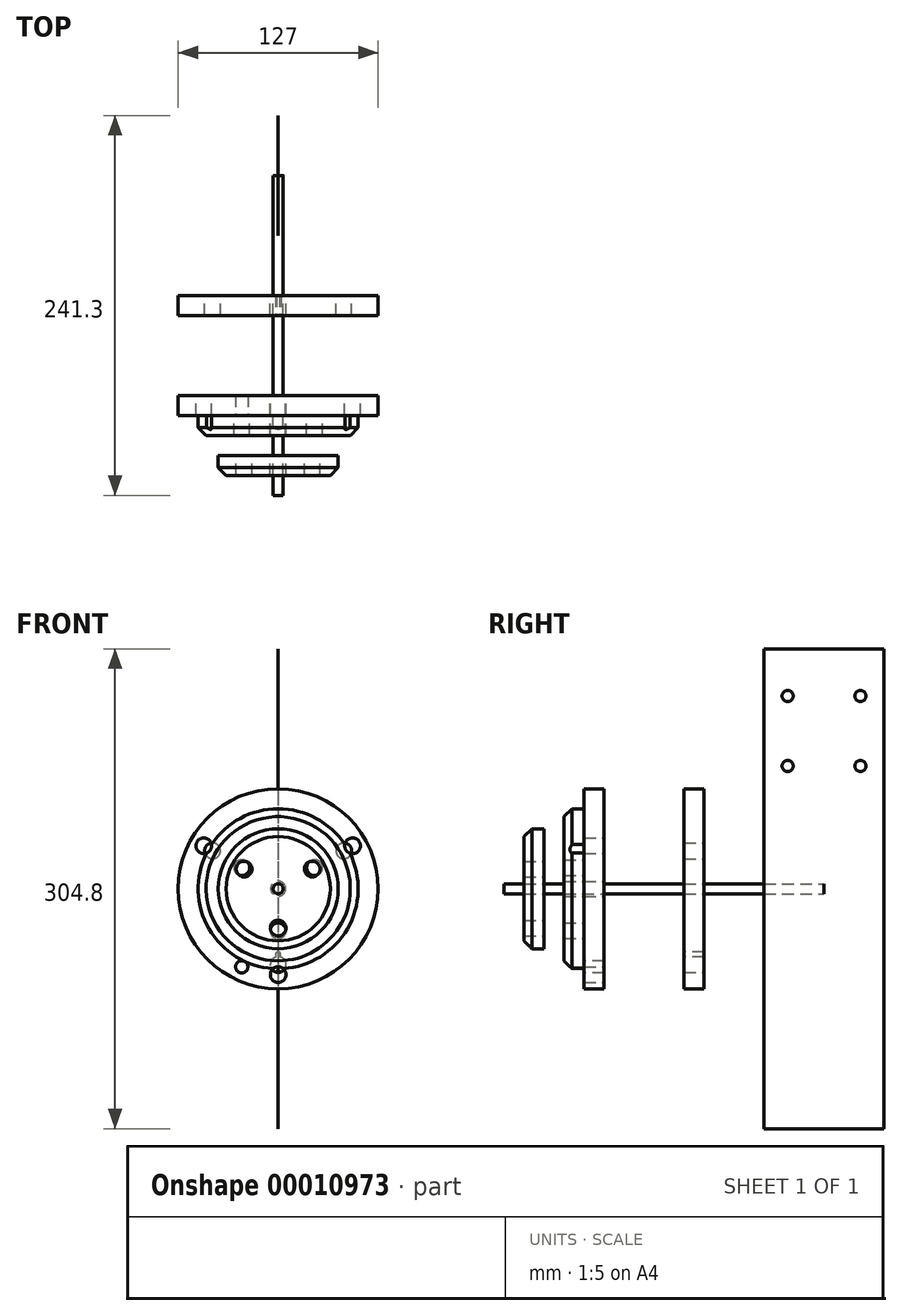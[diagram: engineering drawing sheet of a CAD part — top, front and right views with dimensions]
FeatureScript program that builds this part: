
annotation { "Feature Type Name" : "Feature", "Feature Type Description" : "" }
export const myFeature = defineFeature(function(context is Context, id is Id, definition is map)
    precondition{}
    {
        {
            var Q0;
            Q0=qCreatedBy(makeId("Right.planeOp"),FACE);
            var sketch = newSketch(context, id + "F0", { "sketchPlane" : qUnion([Q0])});
            skLineSegment(sketch, "E0.rect.bottom", {"start": v(-38.1, 152.4) * mm, "end": v(38.1, 152.4) * mm});
            skLineSegment(sketch, "E0.rect.top", {"start": v(-38.1, -152.4) * mm, "end": v(38.1, -152.4) * mm});
            skLineSegment(sketch, "E0.rect.left", {"start": v(-38.1, 152.4) * mm, "end": v(-38.1, -152.4) * mm});
            skLineSegment(sketch, "E0.rect.right", {"start": v(38.1, 152.4) * mm, "end": v(38.1, -152.4) * mm});
            skPoint(sketch, "E0.rect.middle", {"position": v(0, 0) * mm});
            skLineSegment(sketch, "E1", {"start": v(-38.1, 122.4) * mm, "end": v(38.1, 122.4) * mm, "construction": true});
            skCircle(sketch, "E2", {"center": v(-23.1, 122.4) * mm, "radius": 3.56 * mm});
            skCircle(sketch, "E3", {"center": v(23.1, 122.4) * mm, "radius": 3.56 * mm});
            skCircle(sketch, "E4.0.1.0", {"center": v(-23.1, 77.95) * mm, "radius": 3.56 * mm});
            skCircle(sketch, "E4.0.1.1", {"center": v(23.1, 77.95) * mm, "radius": 3.56 * mm});
            skLineSegment(sketch, "E4.direction1", {"start": v(-23.1, 122.4) * mm, "end": v(1.9, 122.4) * mm, "construction": true});
            skLineSegment(sketch, "E4.direction2", {"start": v(-23.1, 122.4) * mm, "end": v(-23.1, 77.95) * mm, "construction": true});
            skSolve(sketch);
        }
        {
            var Q0;
            Q0=makeQuery(id+"F0.imprint","IMPRINT",FACE,{"disambiguationData":[TD([[makeQuery(id+"F0.imprint","IMPRINT",EDGE,{"derivedFrom":sQuery(id+"F0.wireOp",EDGE,"E0.rect.bottom")}),-1.0]])]});
            extrude(context, id + "F1", {"entities" : qUnion([Q0]), "endBound" : BoundingType.SYMMETRIC, "depth" : 1 / 101.6 * mm});
        }
        {
            var Q0;
            Q0=qCreatedBy(makeId("Front.planeOp"),FACE);
            var sketch = newSketch(context, id + "F2", { "sketchPlane" : qUnion([Q0])});
            skCircle(sketch, "E5", {"center": v(0, 0) * mm, "radius": 3.18 * mm});
            skSolve(sketch);
        }
        {
            var Q0;
            Q0 = qSketchRegion(id + "F2", true);
            extrude(context, id + "F3", {"entities" : qUnion([Q0]), "depth" : 203.2 * mm});
        }
        {
            var Q0;
            Q0=qCreatedBy(makeId("Front.planeOp"),FACE);
            cPlane(context, id + "F4", {"entities" : qUnion([Q0]), "cplaneType" : CPlaneType.OFFSET, "offset" : 76.2 * mm, "width" : 150 * mm, "height" : 150 * mm});
        }
        {
            var Q0;
            Q0=qCreatedBy(id+"F4.planeOp",FACE);
            var sketch = newSketch(context, id + "F5", { "sketchPlane" : qUnion([Q0])});
            skCircle(sketch, "E6.0", {"center": v(0, 0) * mm, "radius": 3.18 * mm});
            skCircle(sketch, "E7", {"center": v(0, 0) * mm, "radius": 63.5 * mm});
            skCircle(sketch, "E8", {"center": v(0, -48.15) * mm, "radius": 5 * mm});
            skCircle(sketch, "E9.1.0", {"center": v(41.7, 24.07) * mm, "radius": 5 * mm});
            skCircle(sketch, "E9.2.0", {"center": v(-41.7, 24.07) * mm, "radius": 5 * mm});
            skSolve(sketch);
        }
        {
            var Q0;
            Q0=makeQuery(id+"F5.imprint","IMPRINT",FACE,{"disambiguationData":[TD([[makeQuery(id+"F5.imprint","IMPRINT",EDGE,{"derivedFrom":sQuery(id+"F5.wireOp",EDGE,"E6.0")}),-1.0]])]});
            extrude(context, id + "F6", {"entities" : qUnion([Q0]), "depth" : 12.7 * mm});
        }
        {
            var Q0;
            Q0=makeQuery(id+"F6.opExtrude","CAP_FACE",FACE,{"disambiguationData":[OSD([sQuery(id+"F5.wireOp",EDGE,"E6.0"),sQuery(id+"F5.wireOp",EDGE,"E7")])],"isStart":false});
            cPlane(context, id + "F7", {"entities" : qUnion([Q0]), "cplaneType" : CPlaneType.OFFSET, "offset" : 12.7 * mm, "width" : 150 * mm, "height" : 150 * mm});
        }
        {
            var Q0;
            Q0=qCreatedBy(id+"F7.planeOp",FACE);
            cPlane(context, id + "F8", {"entities" : qUnion([Q0]), "cplaneType" : CPlaneType.OFFSET, "offset" : 76.2 * mm, "width" : 150 * mm, "height" : 150 * mm});
        }
        {
            var Q0;
            Q0=qCreatedBy(id+"F8.planeOp",FACE);
            var sketch = newSketch(context, id + "F9", { "sketchPlane" : qUnion([Q0])});
            skCircle(sketch, "E10.0", {"center": v(0, 0) * mm, "radius": 3.18 * mm});
            skCircle(sketch, "E11", {"center": v(0, 0) * mm, "radius": 38.1 * mm});
            skCircle(sketch, "E12", {"center": v(0, -24.97) * mm, "radius": 5 * mm});
            skCircle(sketch, "E13.1.0", {"center": v(21.63, 12.49) * mm, "radius": 5 * mm});
            skCircle(sketch, "E13.2.0", {"center": v(-21.63, 12.49) * mm, "radius": 5 * mm});
            skSolve(sketch);
        }
        {
            var Q0;
            Q0=makeQuery(id+"F9.imprint","IMPRINT",FACE,{"disambiguationData":[TD([[makeQuery(id+"F9.imprint","IMPRINT",EDGE,{"derivedFrom":sQuery(id+"F9.wireOp",EDGE,"E10.0")}),-1.0]])]});
            extrude(context, id + "F10", {"entities" : qUnion([Q0]), "depth" : 12.7 * mm});
        }
        {
            var Q0;
            Q0=qCreatedBy(id+"F7.planeOp",FACE);
            cPlane(context, id + "F11", {"entities" : qUnion([Q0]), "cplaneType" : CPlaneType.OFFSET, "offset" : 38.1 * mm, "width" : 150 * mm, "height" : 150 * mm});
        }
        {
            var Q0;
            Q0=qCreatedBy(id+"F11.planeOp",FACE);
            var sketch = newSketch(context, id + "F12", { "sketchPlane" : qUnion([Q0])});
            skCircle(sketch, "E14.0", {"center": v(0, 0) * mm, "radius": 3.18 * mm, "construction": true});
            skCircle(sketch, "E15", {"center": v(0, 0) * mm, "radius": 63.5 * mm});
            skCircle(sketch, "E16", {"center": v(0, 0) * mm, "radius": 4.76 * mm});
            skCircle(sketch, "E17", {"center": v(0, -54.56) * mm, "radius": 5 * mm});
            skCircle(sketch, "E18.1.0", {"center": v(47.25, 27.28) * mm, "radius": 5 * mm});
            skCircle(sketch, "E18.2.0", {"center": v(-47.25, 27.28) * mm, "radius": 5 * mm});
            skSolve(sketch);
        }
        {
            var Q0;
            Q0=makeQuery(id+"F12.imprint","IMPRINT",FACE,{"disambiguationData":[TD([[makeQuery(id+"F12.imprint","IMPRINT",EDGE,{"derivedFrom":sQuery(id+"F12.wireOp",EDGE,"E15")}),1.0]])]});
            var Q1;
            Q1=makeQuery(id+"F12.imprint","IMPRINT",FACE,{"disambiguationData":[TD([[makeQuery(id+"F12.imprint","IMPRINT",EDGE,{"derivedFrom":sQuery(id+"F12.wireOp",EDGE,"E14.0")}),-1.0]])]});
            var Q2;
            Q2=makeQuery(id+"F12.imprint","IMPRINT",FACE,{"disambiguationData":[TD([[makeQuery(id+"F12.imprint","IMPRINT",EDGE,{"derivedFrom":sQuery(id+"F12.wireOp",EDGE,"f8c383c6-29e2-4e6e-9d5f-bca426fe2fa6")}),1.0]])]});
            extrude(context, id + "F13", {"entities" : qUnion([Q0, Q1, Q2]), "depth" : 12.7 * mm});
        }
        {
            var Q0;
            Q0=makeQuery(id+"F13.opExtrude","CAP_FACE",FACE,{"disambiguationData":[OSD([sQuery(id+"F12.wireOp",EDGE,"E14.0"),sQuery(id+"F12.wireOp",EDGE,"E15")])],"isStart":false});
            var sketch = newSketch(context, id + "F14", { "sketchPlane" : qUnion([Q0])});
            skCircle(sketch, "E19.0", {"center": v(0, 0) * mm, "radius": 3.18 * mm, "construction": true});
            skCircle(sketch, "E20", {"center": v(0, 0) * mm, "radius": 50.8 * mm});
            skCircle(sketch, "E21.2", {"center": v(0, 0) * mm, "radius": 4.76 * mm});
            skCircle(sketch, "E22", {"center": v(0, -26.71) * mm, "radius": 5 * mm});
            skCircle(sketch, "E23.1.0", {"center": v(23.13, 13.36) * mm, "radius": 5 * mm});
            skCircle(sketch, "E23.2.0", {"center": v(-23.13, 13.36) * mm, "radius": 5 * mm});
            skSolve(sketch);
        }
        {
            var Q0;
            Q0=makeQuery(id+"F14.imprint","IMPRINT",FACE,{"disambiguationData":[TD([[makeQuery(id+"F14.imprint","IMPRINT",EDGE,{"derivedFrom":sQuery(id+"F14.wireOp",EDGE,"E19.0")}),-1.0]])]});
            var Q1;
            Q1=makeQuery(id+"F14.imprint","IMPRINT",FACE,{"disambiguationData":[TD([[makeQuery(id+"F14.imprint","IMPRINT",EDGE,{"derivedFrom":sQuery(id+"F14.wireOp",EDGE,"E20")}),1.0]])]});
            var Q2;
            Q2=makeQuery(id+"F14.imprint","IMPRINT",FACE,{"disambiguationData":[TD([[makeQuery(id+"F14.imprint","IMPRINT",EDGE,{"derivedFrom":sQuery(id+"F14.wireOp",EDGE,"E21.2")}),-1.0]])]});
            extrude(context, id + "F15", {"entities" : qUnion([Q0, Q1, Q2]), "depth" : 12.7 * mm});
        }
        {
            var Q0;
            Q0=makeQuery(id+"F10.opExtrude","CAP_EDGE",EDGE,{"disambiguationData":[OSD([sQuery(id+"F9.wireOp",EDGE,"E11")])],"isStart":false});
            var Q1;
            Q1=makeQuery(id+"F15.opExtrude","CAP_EDGE",EDGE,{"disambiguationData":[OSD([sQuery(id+"F14.wireOp",EDGE,"E20")])],"isStart":false});
            chamfer(context, id + "F16", {"entities" : qUnion([Q0, Q1]), "width" : 5 * mm, "tangentPropagation" : true});
        }
        {
            var Q0;
            Q0=makeQuery(id+"F6.opExtrude","CAP_FACE",FACE,{"disambiguationData":[OSD([sQuery(id+"F5.wireOp",EDGE,"E6.0"),sQuery(id+"F5.wireOp",EDGE,"E7")])],"isStart":false});
            var sketch = newSketch(context, id + "F17", { "sketchPlane" : qUnion([Q0])});
            skCircle(sketch, "E24", {"center": v(0, -41.83) * mm, "radius": 1.68 * mm});
            skSolve(sketch);
        }
        {
            var Q0;
            Q0=makeQuery(id+"F17.imprint","IMPRINT",FACE,{"disambiguationData":[TD([[makeQuery(id+"F17.imprint","IMPRINT",EDGE,{"derivedFrom":sQuery(id+"F17.wireOp",EDGE,"E24")}),1.0]])]});
            var Q1;
            Q1=makeQuery(id+"F6.opExtrude","CAP_FACE",FACE,{"disambiguationData":[OSD([sQuery(id+"F5.wireOp",EDGE,"E6.0"),sQuery(id+"F5.wireOp",EDGE,"E7")])],"isStart":true});
            extrude(context, id + "F18", {"entities" : qUnion([Q0]), "operationType" : NewBodyOperationType.REMOVE, "endBound" : BoundingType.UP_TO_SURFACE, "oppositeDirection" : true, "endBoundEntityFace" : qUnion([Q1]), "depth" : 25 * mm});
        }
        {
            var Q0;
            Q0=makeQuery(id+"F13.opExtrude","CAP_FACE",FACE,{"disambiguationData":[OSD([sQuery(id+"F12.wireOp",EDGE,"E15"),sQuery(id+"F12.wireOp",EDGE,"E16")])],"isStart":false});
            var sketch = newSketch(context, id + "F19", { "sketchPlane" : qUnion([Q0])});
            skCircle(sketch, "E25", {"center": v(-23.15, -49.6) * mm, "radius": 3.9 * mm});
            skSolve(sketch);
        }
        {
            var Q0;
            Q0 = qSketchRegion(id + "F19", true);
            var Q1;
            Q1=makeQuery(id+"F13.opExtrude","CAP_FACE",FACE,{"disambiguationData":[OSD([sQuery(id+"F12.wireOp",EDGE,"E15"),sQuery(id+"F12.wireOp",EDGE,"E16")])],"isStart":true});
            extrude(context, id + "F20", {"entities" : qUnion([Q0]), "operationType" : NewBodyOperationType.REMOVE, "endBound" : BoundingType.UP_TO_SURFACE, "oppositeDirection" : true, "endBoundEntityFace" : qUnion([Q1]), "depth" : 25 * mm});
        }
    });
